# Revit family: RBA5600-001-202W
name_source: partatom
category: Plumbing Fixtures
units: mm (PartAtom-declared; Revit-internal decimal feet)

## family parameters
Always vertical = Yes
Cut with Voids When Loaded = No
OmniClass Number = 23.45.00.00
OmniClass Title = Sanitary, Laundry, and Cleaning Equipment
Part Type = Normal
Room Calculation Point = No
Round Connector Dimension = Use Diameter
Shared = No
Work Plane-Based = No

## types (1)
- RBA5600-001-202W
    Assembly Code = 1300 788 778
    CW Connection = Yes
    Default Elevation = 0 mm  [stored 0 ft]
    Description = Bariatric Toilet
    HW Connection = No
    Keynote = 1300 788 778
    Manufacturer = RBA Group
    Materials & Finishes = 1.5mm #304 Stainless Steel White Polyurethane Finish
    Model = RBA8851-137
    Modified Issue = 20200109.01
    P Trap = Yes
    S Trap = No
    URL = https://www.rba.com.au
    Vent Connection = No
    Waste Connection = Yes

note: [stored X ft] marks values corroborated as IEEE doubles in the binary element streams (Revit-internal decimal feet)

## geometry (parser evidence)
native form markers: Blend x6, Sweep x5
no freeform markers — native parametric forms only
